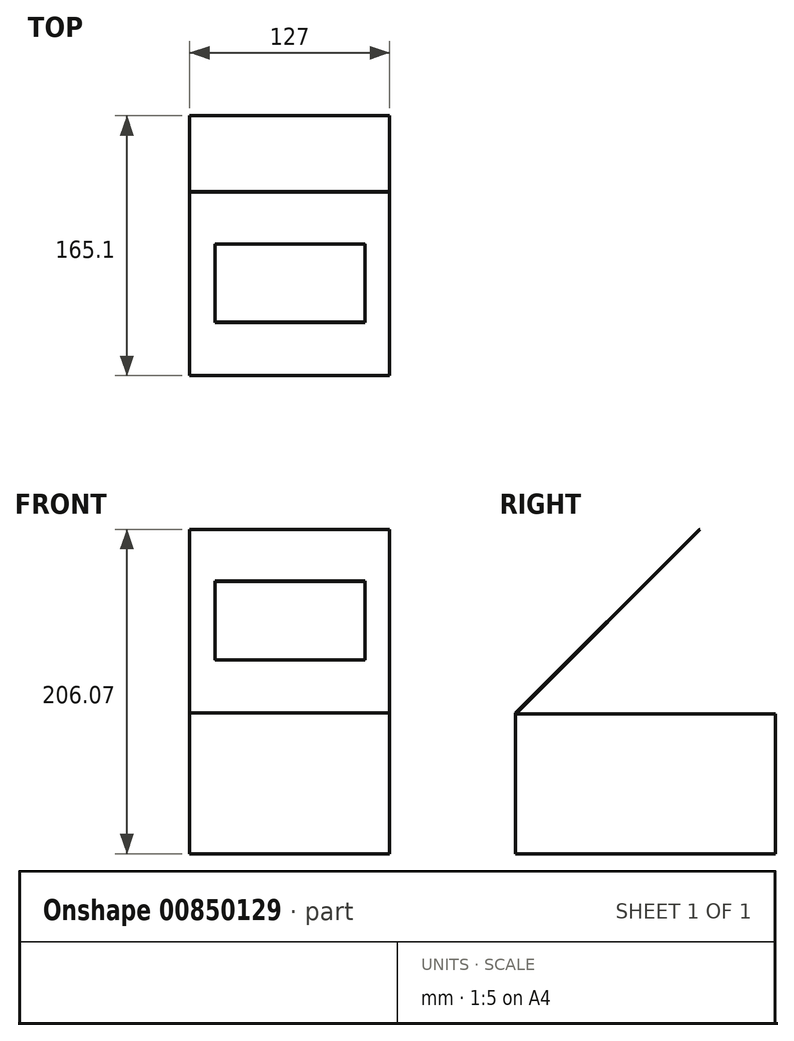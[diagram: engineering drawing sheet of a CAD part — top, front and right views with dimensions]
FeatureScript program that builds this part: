
annotation { "Feature Type Name" : "Feature", "Feature Type Description" : "" }
export const myFeature = defineFeature(function(context is Context, id is Id, definition is map)
    precondition{}
    {
        {
            var Q0;
            Q0=qCreatedBy(makeId("Right.planeOp"),FACE);
            var sketch = newSketch(context, id + "F0", { "sketchPlane" : qUnion([Q0])});
            skLineSegment(sketch, "E0.bottom", {"start": v(0, 0) * mm, "end": v(-165.1, 0) * mm});
            skLineSegment(sketch, "E0.top", {"start": v(0, 88.9) * mm, "end": v(-164.7, 88.9) * mm});
            skLineSegment(sketch, "E0.left", {"start": v(0, 0) * mm, "end": v(0, 88.9) * mm});
            skLineSegment(sketch, "E0.right", {"start": v(-165.1, 0) * mm, "end": v(-165.1, 89.32) * mm});
            skLineSegment(sketch, "E1", {"start": v(-165.1, 89.32) * mm, "end": v(-48.36, 206.07) * mm});
            skLineSegment(sketch, "E2", {"start": v(-48.36, 206.07) * mm, "end": v(-48.07, 205.78) * mm});
            skLineSegment(sketch, "E3", {"start": v(-48.07, 205.78) * mm, "end": v(-164.7, 89.15) * mm});
            skLineSegment(sketch, "E4", {"start": v(-164.7, 88.9) * mm, "end": v(-164.7, 89.15) * mm});
            skLineSegment(sketch, "E5", {"start": v(-164.7, 88.9) * mm, "end": v(-165.1, 88.9) * mm, "construction": true});
            skSolve(sketch);
        }
        {
            var Q0;
            Q0=qSketchRegion(id+"F0",true);
            extrude(context, id + "F1", {"entities" : qUnion([Q0]), "endBound" : BoundingType.SYMMETRIC, "depth" : 127 * mm, "offsetDistance" : 25.4 * mm});
        }
        {
            var Q0;
            Q0=makeQuery(id+"F1.opExtrude","SWEPT_FACE",FACE,{"disambiguationData":[OSD([sQuery(id+"F0.wireOp",EDGE,"E1")])]});
            var sketch = newSketch(context, id + "F2", { "sketchPlane" : qUnion([Q0])});
            skLineSegment(sketch, "E6", {"start": v(-63.39, -52.95) * mm, "end": v(-63.39, 111.36) * mm, "construction": true});
            skLineSegment(sketch, "E7", {"start": v(-63.39, 111.36) * mm, "end": v(63.61, 111.36) * mm, "construction": true});
            skLineSegment(sketch, "E8", {"start": v(63.61, -52.95) * mm, "end": v(63.61, 111.36) * mm, "construction": true});
            skLineSegment(sketch, "E9", {"start": v(-47.51, -5.72) * mm, "end": v(47.74, -5.72) * mm});
            skLineSegment(sketch, "E10", {"start": v(-47.51, 64.92) * mm, "end": v(-47.51, -5.72) * mm});
            skLineSegment(sketch, "E11", {"start": v(47.74, -5.72) * mm, "end": v(47.74, 64.92) * mm});
            skLineSegment(sketch, "E12", {"start": v(47.74, 64.92) * mm, "end": v(-47.51, 64.92) * mm});
            skLineSegment(sketch, "E13", {"start": v(63.61, -52.95) * mm, "end": v(-63.39, -52.95) * mm, "construction": true});
            skSolve(sketch);
        }
        {
            var Q0;
            Q0=qSketchRegion(id+"F2",true);
            var Q1;
            Q1=makeQuery(id+"F1.opExtrude","SWEPT_FACE",FACE,{"disambiguationData":[OSD([sQuery(id+"F0.wireOp",EDGE,"E3")])]});
            extrude(context, id + "F3", {"entities" : qUnion([Q0]), "operationType" : NewBodyOperationType.REMOVE, "endBound" : BoundingType.UP_TO_SURFACE, "oppositeDirection" : true, "depth" : 25.4 * mm, "endBoundEntityFace" : qUnion([Q1]), "offsetDistance" : 25.4 * mm});
        }
    });
